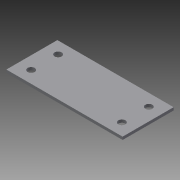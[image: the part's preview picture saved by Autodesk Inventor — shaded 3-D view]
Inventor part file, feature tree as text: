
AUTODESK INVENTOR PART (.ipt)
format: ipt  version: 2014 (Build 180170000, 170)  size: 79,872 bytes
history: native  units: in
note: dims shown in document units (in); Inventor stores cm internally (conversion verified against a paired STEP export)
features: extrude x1, sketch x1
ambient origin geometry x8: Origin, YZ Plane, XZ Plane, XY Plane, X Axis, Y Axis, Z Axis, Center Point
bodies: Solid1 (feature_tree)
feature tree (2):
  extrude  "Extrusion1"  Depth=2.25in
  sketch  "Sketch1"  dims[d0=5.125in d1=2.25in d2=2.0in d3=0.5938in d4=0.3125in d5=0.125in d6=0.0in]
